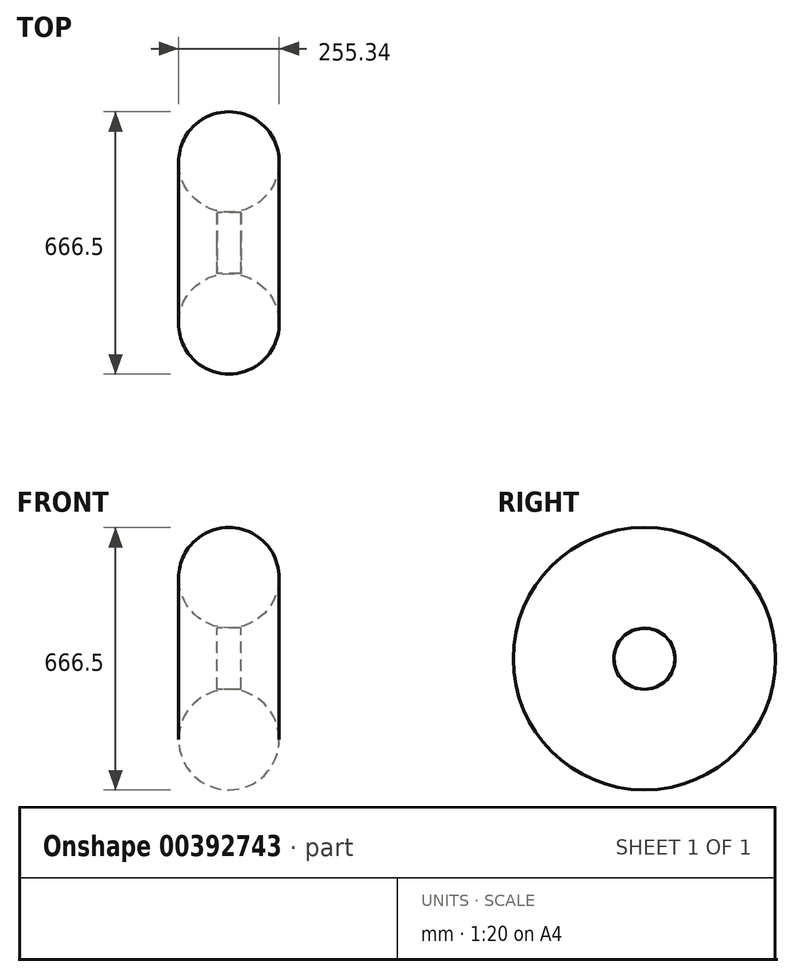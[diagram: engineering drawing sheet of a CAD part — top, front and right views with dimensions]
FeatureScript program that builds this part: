
annotation { "Feature Type Name" : "Feature", "Feature Type Description" : "" }
export const myFeature = defineFeature(function(context is Context, id is Id, definition is map)
    precondition{}
    {
        {
            var Q0;
            Q0=qCreatedBy(makeId("Front.planeOp"),FACE);
            var sketch = newSketch(context, id + "F0", { "sketchPlane" : qUnion([Q0])});
            skCircle(sketch, "E0", {"center": v(0, 128.5) * mm, "radius": 127.67 * mm});
            skLineSegment(sketch, "E1", {"start": v(75.53, -77.08) * mm, "end": v(-76, -77.08) * mm});
            skSolve(sketch);
        }
        {
            var Q0;
            Q0 = qSketchRegion(id + "F0", true);
            var Q1;
            Q1=sQuery(id+"F0.wireOp",EDGE,"E1");
            revolve(context, id + "F1", {"entities" : qUnion([Q0]), "axis" : qUnion([Q1]), "revolveType" : RevolveType.FULL});
        }
        {
            var Q0;
            Q0=qCreatedBy(makeId("Right.planeOp"),FACE);
            var sketch = newSketch(context, id + "F2", { "sketchPlane" : qUnion([Q0])});
            skCircle(sketch, "E2", {"center": v(0, -77) * mm, "radius": 77.67 * mm});
            skSolve(sketch);
        }
        {
            var Q0;
            Q0 = qSketchRegion(id + "F2", true);
            extrude(context, id + "F3", {"entities" : qUnion([Q0]), "endBound" : BoundingType.SYMMETRIC, "depth" : 60.96 * mm});
        }
    });
